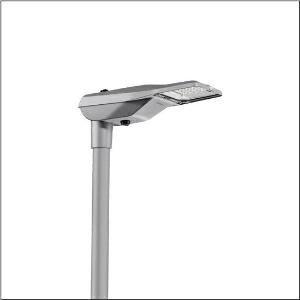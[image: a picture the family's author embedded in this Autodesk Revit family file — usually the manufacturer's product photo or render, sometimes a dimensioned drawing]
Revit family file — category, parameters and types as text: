
# Revit family: streetlight_sl_21_iq_micro___p0_8ab_5xe1r31y08db_c2fe
name_source: partatom
category: Lighting Fixtures
units: mm (PartAtom-declared; Revit-internal decimal feet)

## family parameters
Cut with Voids When Loaded = No
Host = Face
Light Source = No
Part Type = Normal
Room Calculation Point = No
Round Connector Dimension = Use Diameter
Shared = No

## types (1)
- --- (1 x LED, 4550 lm, 39.1 W, 3000K)
    Apparent Load = 39 VA
    CIE Flux Codes = 36 71 98 100 100
    Color Rendering = 70
    Color Temperature = 3000K
    Default Elevation = 1800 mm
    Description = Streetlight SL 21 iQ micro, mast luminaire, primary light control with lens, of PMMA, primary optical cover: cover, of toughened safety glass, transparent, light distribution: P0.8aB, light emission: direct distribution, primary light characteristic: asymmetric, installation type: post-top, side-entry, LED, High Power LED, rated luminous flux: 4.550lm, luminous efficacy: 116lm/W, light colour: 730, colour temperature: 3000K, control gear: iQ-Street Remote, D4i with power reduction, control: pre-setting: logarithmic dimming characteristic, Street-Remote, Auto-Match, Temp-Guard, Lumen-Switch, Night-Set, Smart-Wire, Light-Fading, Desk-Remote (wireless, voltage-free reading and setting of iQ features in the workshop via application-optimized NFC function/RFID function), optimised constant luminous flux control (CLO 2.0), mains connection: 220..240V, AC, 50/60Hz, start of lifetime: 39W, end of service life: 41W, reduction: 17W, luminaire housing, of diecast aluminium, powder-coated, Siteco® metallic grey (DB 702S), corrosivity category C5 high according to DIN EN ISO 12944, please order mast flange separately, inclination adjustable: 0°, 5°, 10°, 15°, sealing non-destructively replaceable, multi-level sealing system, length: 528mm, width: 235mm, height: 110mm, mast flange for spigot size: 42mm (side-entry): 5XC10008XM4, 60/48mm (side-entry/post-top): 5XC10108XM2, 76/60mm (side-entry/post-top): 5XC10108XM1, mounting height: 4..8m, Smart Interface below and above, protection rating (complete): IP66, insulation class (complete): insulation class II (safety insulation), certification: CE, ENEC, ENEC+, VDE, impact resistance: IK10, permissible operating ambient temperature for outdoor applications: -40..+50°C, standard-compliant lighting for roads and squares, packaging unit: 1 piece

Light Distribution: P0.8aB
    Height = 110 mm
    Lamp = 1 x LED
    Lamp Light Flux = 4550 lm
    Lamp Power = 39.1 W
    Lamp count = 1
    Length = 528 mm
    Luminous efficacy = 116 lm/W
    Manufacturer = Siteco
    ModVariant = No
    Model = 5XE1R31Y08DB
    Number of Poles = 1
    OnlyDefault = Yes
    Power Factor = 1
    Product Name = Streetlight SL 21 iQ micro | P0.8aB
    Product group = mast luminaire | pylon top
    ProductGroupID = 6100
    Protection Class = Protection class II
    Protection Degree = IP 66
    RLX_Detail_Level = 1
    RLX_Emergency_Light_Flux = 0 lm
    RLX_Emergency_Type = 0
    RLX_Emergency_Type_DB = No
    RlxData = <blob elided: 98753 chars, md5=7dff5b6d>
    Socket = socket
    Standby Power = 0 W
    System Light Flux = 4550 lm
    System Power = 39 W
    Type Comments = factory setting: luminous flux: 100 % | dim-lin: 254 | 765 mA
    Type Image = l_1007239.jpg
    URL = http://relux.com
    VarID = @adj_085963
    Voltage = 0 V
    Weight = 0.00 kg
    Width = 235 mm

## geometry (parser evidence)
native form markers: Blend x4, Sweep x8
no freeform markers — native parametric forms only
